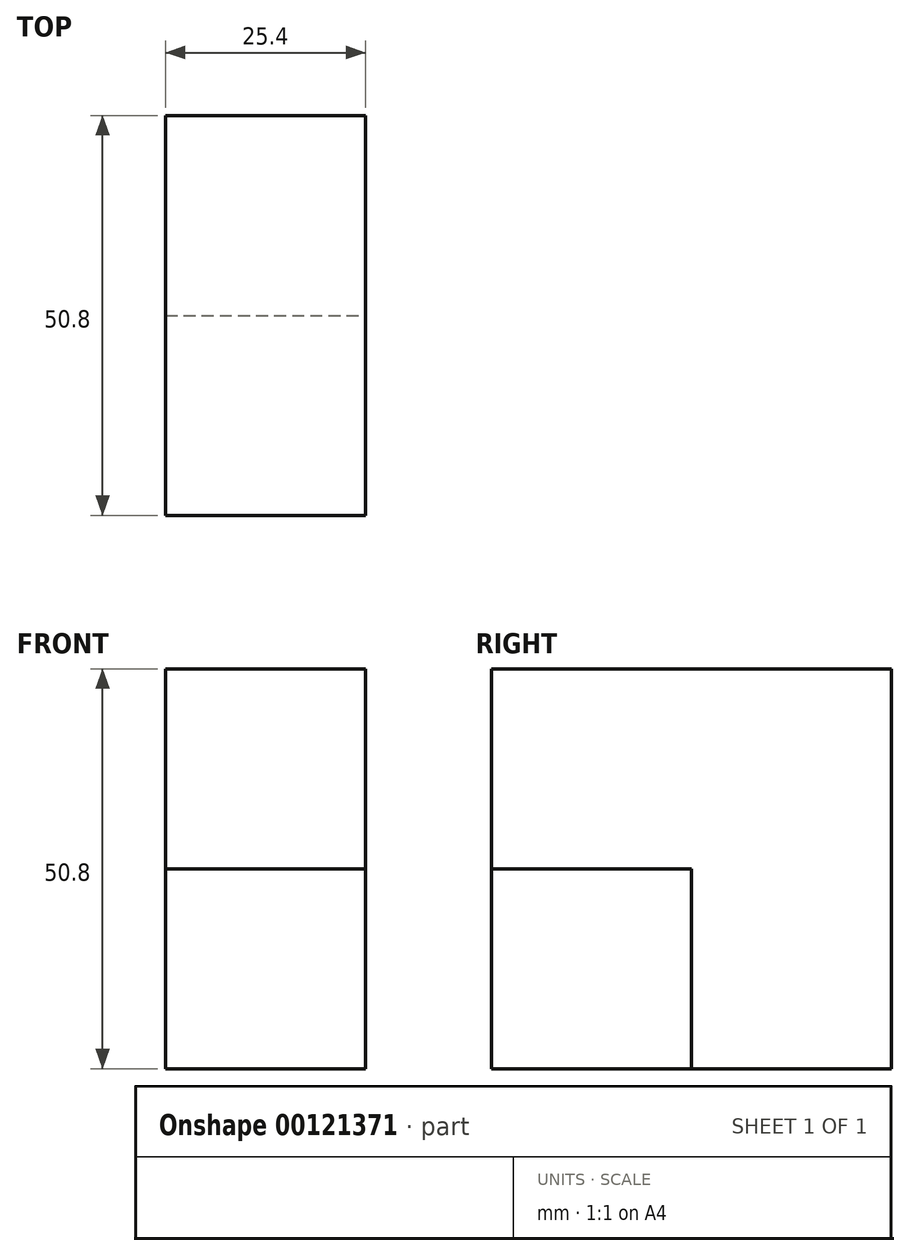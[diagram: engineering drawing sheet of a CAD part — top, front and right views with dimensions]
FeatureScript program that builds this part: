
annotation { "Feature Type Name" : "Feature", "Feature Type Description" : "" }
export const myFeature = defineFeature(function(context is Context, id is Id, definition is map)
    precondition{}
    {
        {
            var Q0;
            Q0=qCreatedBy(makeId("Front.planeOp"),FACE);
            var sketch = newSketch(context, id + "F0", { "sketchPlane" : qUnion([Q0])});
            skLineSegment(sketch, "E0.bottom", {"start": v(0, 0) * mm, "end": v(25.4, 0) * mm});
            skLineSegment(sketch, "E0.top", {"start": v(0, 50.8) * mm, "end": v(25.4, 50.8) * mm});
            skLineSegment(sketch, "E0.left", {"start": v(0, 0) * mm, "end": v(0, 50.8) * mm});
            skLineSegment(sketch, "E0.right", {"start": v(25.4, 0) * mm, "end": v(25.4, 50.8) * mm});
            skSolve(sketch);
        }
        {
            var Q0;
            Q0=makeQuery(id+"F0.imprint","IMPRINT",FACE,{"disambiguationData":[TD([[makeQuery(id+"F0.imprint","IMPRINT",EDGE,{"derivedFrom":sQuery(id+"F0.wireOp",EDGE,"E0.bottom")}),1.0]])]});
            extrude(context, id + "F1", {"entities" : qUnion([Q0]), "depth" : 25.4 * mm});
        }
        {
            var Q0;
            Q0=makeQuery(id+"F1.opExtrude","CAP_FACE",FACE,{"disambiguationData":[OSD([sQuery(id+"F0.wireOp",EDGE,"E0.bottom"),sQuery(id+"F0.wireOp",EDGE,"E0.top"),sQuery(id+"F0.wireOp",EDGE,"E0.left"),sQuery(id+"F0.wireOp",EDGE,"E0.right")])],"isStart":false});
            var sketch = newSketch(context, id + "F2", { "sketchPlane" : qUnion([Q0])});
            skLineSegment(sketch, "E1.bottom", {"start": v(0, 50.8) * mm, "end": v(25.4, 50.8) * mm});
            skLineSegment(sketch, "E1.top", {"start": v(0, 25.4) * mm, "end": v(25.4, 25.4) * mm});
            skLineSegment(sketch, "E1.left", {"start": v(0, 50.8) * mm, "end": v(0, 25.4) * mm});
            skLineSegment(sketch, "E1.right", {"start": v(25.4, 50.8) * mm, "end": v(25.4, 25.4) * mm});
            skSolve(sketch);
        }
        {
            var Q0;
            Q0=makeQuery(id+"F2.imprint","IMPRINT",FACE,{"disambiguationData":[TD([[makeQuery(id+"F2.imprint","IMPRINT",EDGE,{"derivedFrom":sQuery(id+"F2.wireOp",EDGE,"E1.bottom")}),-1.0]])]});
            extrude(context, id + "F3", {"entities" : qUnion([Q0]), "operationType" : NewBodyOperationType.ADD, "depth" : 25.4 * mm});
        }
        {
            var Q0;
            Q0=makeQuery(id+"F3.boolean.opBoolean","MERGE",FACE,{"derivedFrom":[makeQuery(id+"F1.opExtrude","SWEPT_FACE",FACE,{"disambiguationData":[OSD([sQuery(id+"F0.wireOp",EDGE,"E0.right")])]}),makeQuery(id+"F3.opExtrude","SWEPT_FACE",FACE,{"disambiguationData":[OSD([sQuery(id+"F2.wireOp",EDGE,"E1.right")])]})]});
            var sketch = newSketch(context, id + "F4", { "sketchPlane" : qUnion([Q0])});
            skLineSegment(sketch, "E2.bottom", {"start": v(-50.8, 25.4) * mm, "end": v(-25.4, 25.4) * mm});
            skLineSegment(sketch, "E2.top", {"start": v(-50.8, 0) * mm, "end": v(-25.4, 0) * mm});
            skLineSegment(sketch, "E2.left", {"start": v(-50.8, 25.4) * mm, "end": v(-50.8, 0) * mm});
            skLineSegment(sketch, "E2.right", {"start": v(-25.4, 25.4) * mm, "end": v(-25.4, 0) * mm});
            skSolve(sketch);
        }
        {
            var Q0;
            Q0=makeQuery(id+"F4.imprint","IMPRINT",FACE,{"disambiguationData":[TD([[makeQuery(id+"F4.imprint","IMPRINT",EDGE,{"derivedFrom":sQuery(id+"F4.wireOp",EDGE,"E2.bottom")}),-1.0]])]});
            extrude(context, id + "F5", {"entities" : qUnion([Q0]), "oppositeDirection" : true, "depth" : 25.4 * mm});
        }
    });
